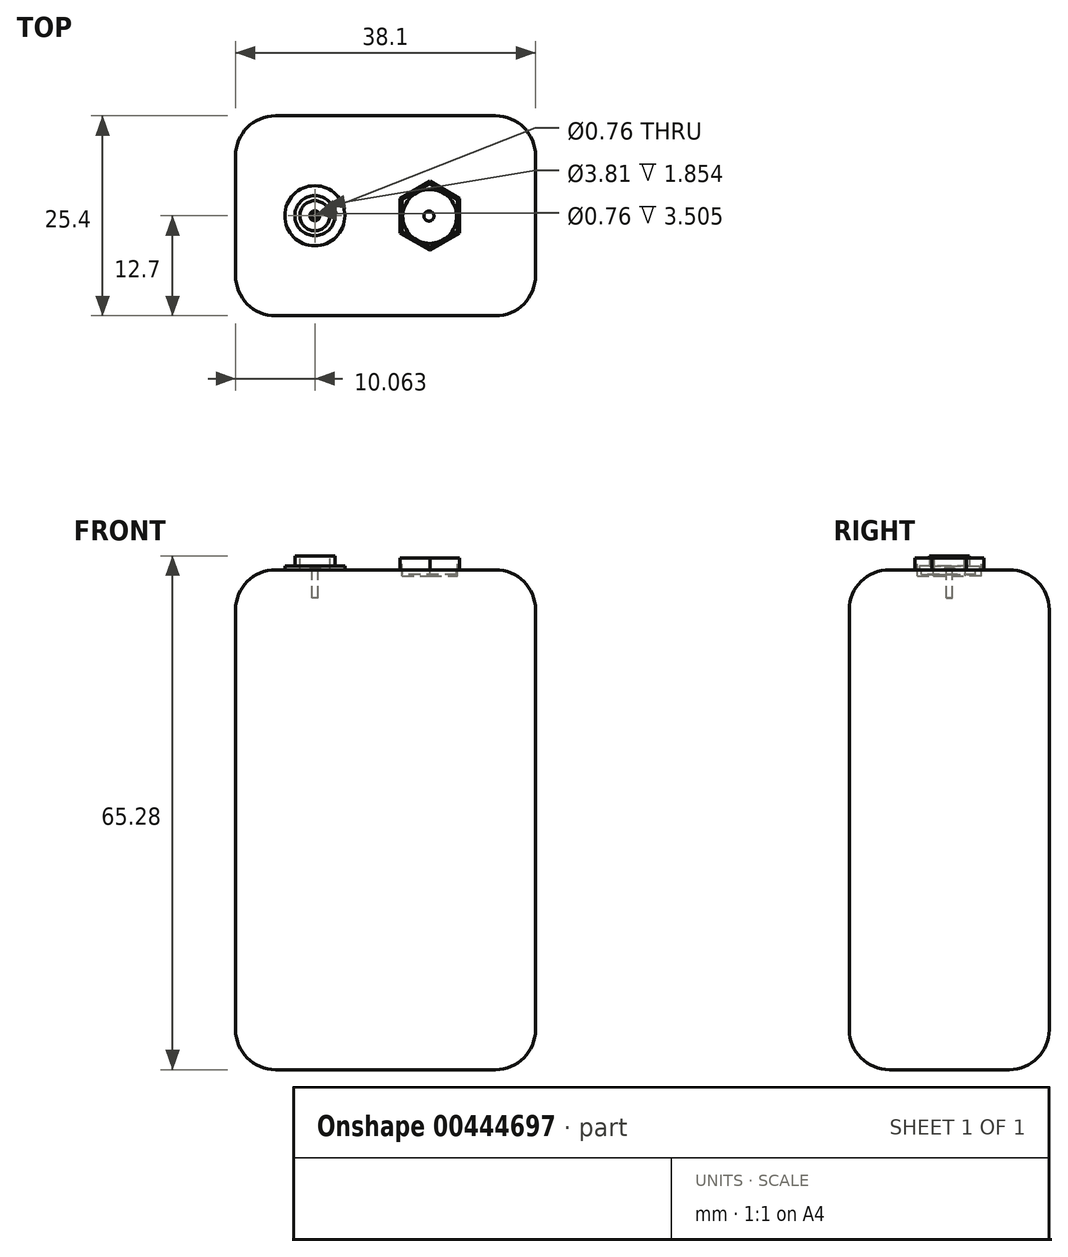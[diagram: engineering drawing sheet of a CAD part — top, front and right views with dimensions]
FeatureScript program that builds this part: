
annotation { "Feature Type Name" : "Feature", "Feature Type Description" : "" }
export const myFeature = defineFeature(function(context is Context, id is Id, definition is map)
    precondition{}
    {
        {
            var Q0;
            Q0=qCreatedBy(makeId("Front.planeOp"),FACE);
            var sketch = newSketch(context, id + "F0", { "sketchPlane" : qUnion([Q0])});
            skLineSegment(sketch, "E0.bottom", {"start": v(19.05, 31.75) * mm, "end": v(-19.05, 31.75) * mm});
            skLineSegment(sketch, "E0.top", {"start": v(19.05, -31.75) * mm, "end": v(-19.05, -31.75) * mm});
            skLineSegment(sketch, "E0.left", {"start": v(19.05, 31.75) * mm, "end": v(19.05, -31.75) * mm});
            skLineSegment(sketch, "E0.right", {"start": v(-19.05, 31.75) * mm, "end": v(-19.05, -31.75) * mm});
            skPoint(sketch, "E0.middle", {"position": v(0, 0) * mm});
            skSolve(sketch);
        }
        {
            var Q0;
            Q0=makeQuery(id+"F0.imprint","IMPRINT",FACE,{"disambiguationData":[TD([[makeQuery(id+"F0.imprint","IMPRINT",EDGE,{"derivedFrom":sQuery(id+"F0.wireOp",EDGE,"E0.bottom")}),1.0]])]});
            extrude(context, id + "F1", {"entities" : qUnion([Q0]), "depth" : 25.4 * mm});
        }
        {
            var Q0;
            Q0=makeQuery(id+"F1.opExtrude","CAP_FACE",FACE,{"disambiguationData":[OSD([sQuery(id+"F0.wireOp",EDGE,"E0.bottom"),sQuery(id+"F0.wireOp",EDGE,"E0.top"),sQuery(id+"F0.wireOp",EDGE,"E0.left"),sQuery(id+"F0.wireOp",EDGE,"E0.right")])],"isStart":false});
            var Q1;
            Q1=makeQuery(id+"F1.opExtrude","SWEPT_FACE",FACE,{"disambiguationData":[OSD([sQuery(id+"F0.wireOp",EDGE,"E0.left")])]});
            var Q2;
            Q2=makeQuery(id+"F1.opExtrude","CAP_FACE",FACE,{"disambiguationData":[OSD([sQuery(id+"F0.wireOp",EDGE,"E0.bottom"),sQuery(id+"F0.wireOp",EDGE,"E0.top"),sQuery(id+"F0.wireOp",EDGE,"E0.left"),sQuery(id+"F0.wireOp",EDGE,"E0.right")])],"isStart":true});
            var Q3;
            Q3=makeQuery(id+"F1.opExtrude","SWEPT_FACE",FACE,{"disambiguationData":[OSD([sQuery(id+"F0.wireOp",EDGE,"E0.right")])]});
            fillet(context, id + "F2", {"entities" : qUnion([Q0, Q1, Q2, Q3]), "radius" : 5.08 * mm, "tangentPropagation" : true, "allowEdgeOverflow" : false});
        }
        {
            var Q0;
            Q0=makeQuery(id+"F1.opExtrude","SWEPT_FACE",FACE,{"disambiguationData":[OSD([sQuery(id+"F0.wireOp",EDGE,"E0.bottom")])]});
            var sketch = newSketch(context, id + "F3", { "sketchPlane" : qUnion([Q0])});
            skCircle(sketch, "E1", {"center": v(-8.99, -12.7) * mm, "radius": 3.8 * mm});
            skSolve(sketch);
        }
        {
            var Q0;
            Q0=makeQuery(id+"F3.imprint","IMPRINT",FACE,{"disambiguationData":[TD([[makeQuery(id+"F3.imprint","IMPRINT",EDGE,{"derivedFrom":sQuery(id+"F3.wireOp",EDGE,"E1")}),1.0]])]});
            extrude(context, id + "F4", {"entities" : qUnion([Q0]), "operationType" : NewBodyOperationType.ADD, "depth" : 0.5 * mm});
        }
        {
            var Q0;
            Q0=makeQuery(id+"F4.opExtrude","CAP_FACE",FACE,{"disambiguationData":[OSD([sQuery(id+"F3.wireOp",EDGE,"E1")])],"isStart":false});
            var sketch = newSketch(context, id + "F5", { "sketchPlane" : qUnion([Q0])});
            skCircle(sketch, "E2", {"center": v(-8.99, -12.7) * mm, "radius": 2.54 * mm});
            skSolve(sketch);
        }
        {
            var Q0;
            Q0=makeQuery(id+"F5.imprint","IMPRINT",FACE,{"disambiguationData":[TD([[makeQuery(id+"F5.imprint","IMPRINT",EDGE,{"derivedFrom":sQuery(id+"F5.wireOp",EDGE,"E2")}),1.0]])]});
            extrude(context, id + "F6", {"entities" : qUnion([Q0]), "operationType" : NewBodyOperationType.ADD, "depth" : 1.27 * mm});
        }
        {
            var Q0;
            Q0=makeQuery(id+"F6.opExtrude","CAP_FACE",FACE,{"disambiguationData":[OSD([sQuery(id+"F5.wireOp",EDGE,"E2")])],"isStart":false});
            var sketch = newSketch(context, id + "F7", { "sketchPlane" : qUnion([Q0])});
            skCircle(sketch, "E3", {"center": v(-8.99, -12.7) * mm, "radius": 1.9 * mm});
            skSolve(sketch);
        }
        {
            var Q0;
            Q0=makeQuery(id+"F7.imprint","IMPRINT",FACE,{"disambiguationData":[TD([[makeQuery(id+"F7.imprint","IMPRINT",EDGE,{"derivedFrom":sQuery(id+"F7.wireOp",EDGE,"E3")}),1.0]])]});
            extrude(context, id + "F8", {"entities" : qUnion([Q0]), "operationType" : NewBodyOperationType.REMOVE, "endBound" : BoundingType.SYMMETRIC, "oppositeDirection" : true, "depth" : 3.7 * mm});
        }
        {
            var Q0;
            Q0=makeQuery(id+"F1.opExtrude","SWEPT_FACE",FACE,{"disambiguationData":[OSD([sQuery(id+"F0.wireOp",EDGE,"E0.bottom")])]});
            var sketch = newSketch(context, id + "F9", { "sketchPlane" : qUnion([Q0])});
            skCircle(sketch, "E4.cCircle", {"center": v(5.62, -12.7) * mm, "radius": 3.78 * mm, "construction": true});
            skLineSegment(sketch, "E4.0", {"start": v(9.4, -10.52) * mm, "end": v(9.4, -14.88) * mm});
            skLineSegment(sketch, "E4.1", {"start": v(9.4, -14.88) * mm, "end": v(5.62, -17.07) * mm});
            skLineSegment(sketch, "E4.2", {"start": v(5.62, -17.07) * mm, "end": v(1.84, -14.88) * mm});
            skLineSegment(sketch, "E4.3", {"start": v(1.84, -14.88) * mm, "end": v(1.84, -10.52) * mm});
            skLineSegment(sketch, "E4.4", {"start": v(1.84, -10.52) * mm, "end": v(5.62, -8.33) * mm});
            skLineSegment(sketch, "E4.5", {"start": v(5.62, -8.33) * mm, "end": v(9.4, -10.52) * mm});
            skPoint(sketch, "E4.0.midPoint", {"position": v(9.4, -12.7) * mm});
            skSolve(sketch);
        }
        {
            var Q0;
            Q0=makeQuery(id+"F9.imprint","IMPRINT",FACE,{"disambiguationData":[TD([[makeQuery(id+"F9.imprint","IMPRINT",EDGE,{"derivedFrom":sQuery(id+"F9.wireOp",EDGE,"E4.0")}),-1.0]])]});
            extrude(context, id + "F10", {"entities" : qUnion([Q0]), "operationType" : NewBodyOperationType.ADD, "depth" : 1.52 * mm});
        }
        {
            var Q0;
            Q0=makeQuery(id+"F10.opExtrude","CAP_FACE",FACE,{"disambiguationData":[OSD([sQuery(id+"F9.wireOp",EDGE,"E4.0"),sQuery(id+"F9.wireOp",EDGE,"E4.1"),sQuery(id+"F9.wireOp",EDGE,"E4.2"),sQuery(id+"F9.wireOp",EDGE,"E4.3"),sQuery(id+"F9.wireOp",EDGE,"E4.4"),sQuery(id+"F9.wireOp",EDGE,"E4.5")])],"isStart":false});
            var sketch = newSketch(context, id + "F11", { "sketchPlane" : qUnion([Q0])});
            skSolve(sketch);
        }
        {
            var Q0;
            Q0=makeQuery(id+"F11.imprint","IMPRINT",FACE,{"disambiguationData":[TD([[makeQuery(id+"F11.imprint","IMPRINT",EDGE,{"derivedFrom":makeQuery(id+"F10.opExtrude","CAP_EDGE",EDGE,{"disambiguationData":[OSD([sQuery(id+"F9.wireOp",EDGE,"E4.0")])],"isStart":false})}),-1.0]])]});
            var sketch = newSketch(context, id + "F12", { "sketchPlane" : qUnion([Q0])});
            skCircle(sketch, "E5.cCircle", {"center": v(5.62, -12.7) * mm, "radius": 3.53 * mm, "construction": true});
            skLineSegment(sketch, "E5.0", {"start": v(5.62, -8.63) * mm, "end": v(9.15, -10.66) * mm});
            skLineSegment(sketch, "E5.1", {"start": v(9.15, -10.66) * mm, "end": v(9.15, -14.74) * mm});
            skLineSegment(sketch, "E5.2", {"start": v(9.15, -14.74) * mm, "end": v(5.62, -16.77) * mm});
            skLineSegment(sketch, "E5.3", {"start": v(5.62, -16.77) * mm, "end": v(2.09, -14.74) * mm});
            skLineSegment(sketch, "E5.4", {"start": v(2.09, -14.74) * mm, "end": v(2.09, -10.66) * mm});
            skLineSegment(sketch, "E5.5", {"start": v(2.09, -10.66) * mm, "end": v(5.62, -8.63) * mm});
            skPoint(sketch, "E5.0.midPoint", {"position": v(7.38, -9.64) * mm});
            skSolve(sketch);
        }
        {
            var Q0;
            Q0=makeQuery(id+"F12.imprint","IMPRINT",FACE,{"disambiguationData":[TD([[makeQuery(id+"F12.imprint","IMPRINT",EDGE,{"derivedFrom":sQuery(id+"F12.wireOp",EDGE,"E5.0")}),-1.0]])]});
            extrude(context, id + "F13", {"entities" : qUnion([Q0]), "operationType" : NewBodyOperationType.REMOVE, "oppositeDirection" : true, "depth" : 2.3 * mm});
        }
        {
            var Q0;
            Q0=makeQuery(id+"F1.opExtrude","SWEPT_FACE",FACE,{"disambiguationData":[OSD([sQuery(id+"F0.wireOp",EDGE,"E0.bottom")])]});
            var sketch = newSketch(context, id + "F14", { "sketchPlane" : qUnion([Q0])});
            skCircle(sketch, "E6", {"center": v(5.6, -12.78) * mm, "radius": 3.43 * mm});
            skSolve(sketch);
        }
        {
            var Q0;
            Q0 = qSketchRegion(id + "F14", true);
            extrude(context, id + "F15", {"entities" : qUnion([Q0]), "oppositeDirection" : true, "depth" : 0.58 * mm});
        }
        {
            var Q0;
            Q0=makeQuery(id+"F1.opExtrude","SWEPT_FACE",FACE,{"disambiguationData":[OSD([sQuery(id+"F0.wireOp",EDGE,"E0.bottom")])]});
            var sketch = newSketch(context, id + "F16", { "sketchPlane" : qUnion([Q0])});
            skCircle(sketch, "E7", {"center": v(5.5, -12.74) * mm, "radius": 0.64 * mm});
            skSolve(sketch);
        }
        {
            var Q0;
            Q0=makeQuery(id+"F16.imprint","IMPRINT",FACE,{"disambiguationData":[TD([[makeQuery(id+"F16.imprint","IMPRINT",EDGE,{"derivedFrom":sQuery(id+"F16.wireOp",EDGE,"E7")}),1.0]])]});
            extrude(context, id + "F17", {"entities" : qUnion([Q0]), "depth" : 0.03 * mm});
        }
        {
            var Q0;
            Q0=makeQuery(id+"F1.opExtrude","SWEPT_FACE",FACE,{"disambiguationData":[OSD([sQuery(id+"F0.wireOp",EDGE,"E0.bottom")])]});
            var sketch = newSketch(context, id + "F18", { "sketchPlane" : qUnion([Q0])});
            skCircle(sketch, "E8", {"center": v(-8.99, -12.7) * mm, "radius": 0.64 * mm});
            skSolve(sketch);
        }
        {
            var Q0;
            Q0=makeQuery(id+"F18.imprint","IMPRINT",FACE,{"disambiguationData":[TD([[makeQuery(id+"F18.imprint","IMPRINT",EDGE,{"derivedFrom":sQuery(id+"F18.wireOp",EDGE,"E8")}),1.0]])]});
            extrude(context, id + "F19", {"entities" : qUnion([Q0]), "depth" : 0.25 * mm});
        }
        {
            var Q0;
            Q0=makeQuery(id+"F19.opExtrude","CAP_FACE",FACE,{"disambiguationData":[OSD([sQuery(id+"F18.wireOp",EDGE,"E8")])],"isStart":false});
            var sketch = newSketch(context, id + "F20", { "sketchPlane" : qUnion([Q0])});
            skCircle(sketch, "E9", {"center": v(-8.99, -12.7) * mm, "radius": 0.38 * mm});
            skSolve(sketch);
        }
        {
            var Q0;
            Q0=makeQuery(id+"F20.imprint","IMPRINT",FACE,{"disambiguationData":[TD([[makeQuery(id+"F20.imprint","IMPRINT",EDGE,{"derivedFrom":sQuery(id+"F20.wireOp",EDGE,"E9")}),1.0]])]});
            extrude(context, id + "F21", {"entities" : qUnion([Q0]), "operationType" : NewBodyOperationType.REMOVE, "oppositeDirection" : true, "depth" : 3.84 * mm});
        }
    });
